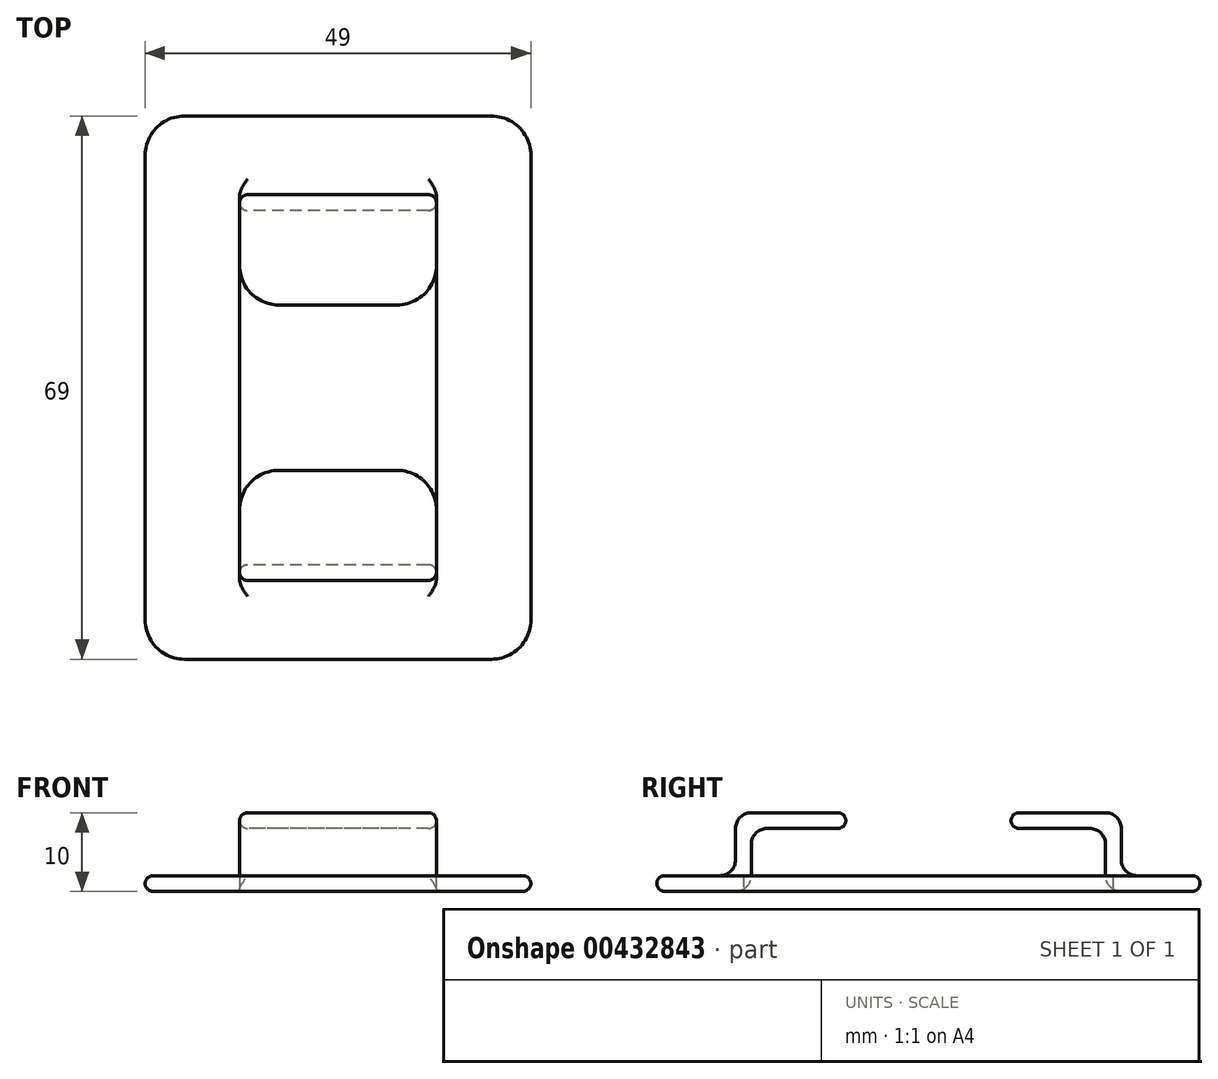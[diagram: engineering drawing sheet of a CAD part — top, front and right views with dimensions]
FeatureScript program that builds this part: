
annotation { "Feature Type Name" : "Feature", "Feature Type Description" : "" }
export const myFeature = defineFeature(function(context is Context, id is Id, definition is map)
    precondition{}
    {
        {
            var Q0;
            Q0=qCreatedBy(makeId("Right.planeOp"),FACE);
            var sketch = newSketch(context, id + "F0", { "sketchPlane" : qUnion([Q0])});
            skLineSegment(sketch, "E0.bottom", {"start": v(22.5, 3) * mm, "end": v(-22.5, 3) * mm, "construction": true});
            skLineSegment(sketch, "E0.top", {"start": v(22.5, -3) * mm, "end": v(-22.5, -3) * mm, "construction": true});
            skLineSegment(sketch, "E0.left", {"start": v(22.5, 3) * mm, "end": v(22.5, -3) * mm, "construction": true});
            skLineSegment(sketch, "E0.right", {"start": v(-22.5, 3) * mm, "end": v(-22.5, -3) * mm, "construction": true});
            skPoint(sketch, "E0.middle", {"position": v(0, 0) * mm});
            skLineSegment(sketch, "E1.bottom", {"start": v(20.5, 3) * mm, "end": v(10.5, 3) * mm});
            skLineSegment(sketch, "E1.top", {"start": v(22.5, 5) * mm, "end": v(10.5, 5) * mm});
            skLineSegment(sketch, "E1.right", {"start": v(10.5, 3) * mm, "end": v(10.5, 5) * mm});
            skLineSegment(sketch, "E2.bottom", {"start": v(-20.5, 3) * mm, "end": v(-10.5, 3) * mm});
            skLineSegment(sketch, "E2.top", {"start": v(-22.5, 5) * mm, "end": v(-10.5, 5) * mm});
            skLineSegment(sketch, "E2.right", {"start": v(-10.5, 3) * mm, "end": v(-10.5, 5) * mm});
            skLineSegment(sketch, "E3.bottom", {"start": v(26.5, -3) * mm, "end": v(34.5, -3) * mm});
            skLineSegment(sketch, "E3.top", {"start": v(24.5, -5) * mm, "end": v(34.5, -5) * mm});
            skLineSegment(sketch, "E3.left", {"start": v(22.5, -3) * mm, "end": v(22.5, -3) * mm});
            skLineSegment(sketch, "E3.right", {"start": v(34.5, -3) * mm, "end": v(34.5, -5) * mm});
            skLineSegment(sketch, "E4.bottom", {"start": v(-26.5, -3) * mm, "end": v(-34.5, -3) * mm});
            skLineSegment(sketch, "E4.top", {"start": v(-24.5, -5) * mm, "end": v(-34.5, -5) * mm});
            skLineSegment(sketch, "E4.left", {"start": v(-22.5, -3) * mm, "end": v(-22.5, -3) * mm});
            skLineSegment(sketch, "E4.right", {"start": v(-34.5, -3) * mm, "end": v(-34.5, -5) * mm});
            skLineSegment(sketch, "E5.bottom", {"start": v(22.5, 5) * mm, "end": v(22.5, 5) * mm});
            skLineSegment(sketch, "E5.left", {"start": v(22.5, 1) * mm, "end": v(22.5, -3) * mm});
            skLineSegment(sketch, "E5.right", {"start": v(24.5, 3) * mm, "end": v(24.5, -1) * mm});
            skLineSegment(sketch, "E6.bottom", {"start": v(-22.5, 5) * mm, "end": v(-22.5, 5) * mm});
            skLineSegment(sketch, "E6.left", {"start": v(-22.5, 1) * mm, "end": v(-22.5, -3) * mm});
            skLineSegment(sketch, "E6.right", {"start": v(-24.5, 3) * mm, "end": v(-24.5, -1) * mm});
            skPoint(sketch, "E7.visualSharp", {"position": v(22.5, 3) * mm});
            skArc(sketch, "E7.filletArc", {"start": v(22.5, 1) * mm, "mid": v(21.91, 2.41) * mm, "end": v(20.5, 3) * mm});
            skPoint(sketch, "E8.visualSharp", {"position": v(24.5, 5) * mm});
            skArc(sketch, "E8.filletArc", {"start": v(24.5, 3) * mm, "mid": v(23.91, 4.41) * mm, "end": v(22.5, 5) * mm});
            skPoint(sketch, "E9.visualSharp", {"position": v(24.5, -3) * mm});
            skArc(sketch, "E9.filletArc", {"start": v(24.5, -1) * mm, "mid": v(25.09, -2.41) * mm, "end": v(26.5, -3) * mm});
            skPoint(sketch, "E10.visualSharp", {"position": v(22.5, -5) * mm});
            skArc(sketch, "E10.filletArc", {"start": v(22.5, -3) * mm, "mid": v(23.09, -4.41) * mm, "end": v(24.5, -5) * mm});
            skPoint(sketch, "E11.visualSharp", {"position": v(-24.5, 5) * mm});
            skArc(sketch, "E11.filletArc", {"start": v(-22.5, 5) * mm, "mid": v(-23.91, 4.41) * mm, "end": v(-24.5, 3) * mm});
            skArc(sketch, "E12.filletArc", {"start": v(-20.5, 3) * mm, "mid": v(-21.91, 2.41) * mm, "end": v(-22.5, 1) * mm});
            skPoint(sketch, "E13.visualSharp", {"position": v(-24.5, -3) * mm});
            skArc(sketch, "E13.filletArc", {"start": v(-26.5, -3) * mm, "mid": v(-25.09, -2.41) * mm, "end": v(-24.5, -1) * mm});
            skPoint(sketch, "E14.visualSharp", {"position": v(-22.5, -5) * mm});
            skArc(sketch, "E14.filletArc", {"start": v(-24.5, -5) * mm, "mid": v(-23.09, -4.41) * mm, "end": v(-22.5, -3) * mm});
            skSolve(sketch);
        }
        {
            var Q0;
            Q0 = qSketchRegion(id + "F0", true);
            extrude(context, id + "F1", {"entities" : qUnion([Q0]), "depth" : 25 * mm});
        }
        {
            var Q0;
            Q0=makeQuery(id+"F1.opExtrude","CAP_FACE",FACE,{"disambiguationData":[OSD([sQuery(id+"F0.wireOp",EDGE,"E2.bottom"),sQuery(id+"F0.wireOp",EDGE,"E2.top"),sQuery(id+"F0.wireOp",EDGE,"E2.right"),sQuery(id+"F0.wireOp",EDGE,"E4.bottom"),sQuery(id+"F0.wireOp",EDGE,"E4.top"),sQuery(id+"F0.wireOp",EDGE,"E4.right"),sQuery(id+"F0.wireOp",EDGE,"E6.left"),sQuery(id+"F0.wireOp",EDGE,"E6.right"),sQuery(id+"F0.wireOp",EDGE,"E11.filletArc"),sQuery(id+"F0.wireOp",EDGE,"E12.filletArc"),sQuery(id+"F0.wireOp",EDGE,"E13.filletArc"),sQuery(id+"F0.wireOp",EDGE,"E14.filletArc")])],"isStart":false});
            var sketch = newSketch(context, id + "F2", { "sketchPlane" : qUnion([Q0])});
            skLineSegment(sketch, "E15.bottom", {"start": v(-34.5, -5) * mm, "end": v(34.5, -5) * mm});
            skLineSegment(sketch, "E15.top", {"start": v(-34.5, -3) * mm, "end": v(34.5, -3) * mm});
            skLineSegment(sketch, "E15.left", {"start": v(-34.5, -5) * mm, "end": v(-34.5, -3) * mm});
            skLineSegment(sketch, "E15.right", {"start": v(34.5, -5) * mm, "end": v(34.5, -3) * mm});
            skSolve(sketch);
        }
        {
            var Q0;
            Q0 = qSketchRegion(id + "F2", true);
            extrude(context, id + "F3", {"entities" : qUnion([Q0]), "operationType" : NewBodyOperationType.ADD, "depth" : 12 * mm});
        }
        {
            var Q0;
            Q0=makeQuery(id+"F1.opExtrude","CAP_FACE",FACE,{"disambiguationData":[OSD([sQuery(id+"F0.wireOp",EDGE,"E1.bottom"),sQuery(id+"F0.wireOp",EDGE,"E1.top"),sQuery(id+"F0.wireOp",EDGE,"E1.right"),sQuery(id+"F0.wireOp",EDGE,"E3.bottom"),sQuery(id+"F0.wireOp",EDGE,"E3.top"),sQuery(id+"F0.wireOp",EDGE,"E3.right"),sQuery(id+"F0.wireOp",EDGE,"E5.left"),sQuery(id+"F0.wireOp",EDGE,"E5.right"),sQuery(id+"F0.wireOp",EDGE,"E7.filletArc"),sQuery(id+"F0.wireOp",EDGE,"E8.filletArc"),sQuery(id+"F0.wireOp",EDGE,"E9.filletArc"),sQuery(id+"F0.wireOp",EDGE,"E10.filletArc")])],"isStart":true});
            var sketch = newSketch(context, id + "F4", { "sketchPlane" : qUnion([Q0])});
            skLineSegment(sketch, "E16.bottom", {"start": v(-34.5, -5) * mm, "end": v(34.5, -5) * mm});
            skLineSegment(sketch, "E16.top", {"start": v(-34.5, -3) * mm, "end": v(34.5, -3) * mm});
            skLineSegment(sketch, "E16.left", {"start": v(-34.5, -5) * mm, "end": v(-34.5, -3) * mm});
            skLineSegment(sketch, "E16.right", {"start": v(34.5, -5) * mm, "end": v(34.5, -3) * mm});
            skSolve(sketch);
        }
        {
            var Q0;
            Q0 = qSketchRegion(id + "F4", true);
            extrude(context, id + "F5", {"entities" : qUnion([Q0]), "operationType" : NewBodyOperationType.ADD, "depth" : 12 * mm});
        }
        {
            var Q0;
            Q0=makeQuery(id+"F5.opExtrude","CAP_EDGE",EDGE,{"disambiguationData":[OSD([sQuery(id+"F4.wireOp",EDGE,"E16.left")])],"isStart":false});
            var Q1;
            Q1=makeQuery(id+"F3.opExtrude","CAP_EDGE",EDGE,{"disambiguationData":[OSD([sQuery(id+"F2.wireOp",EDGE,"E15.right")])],"isStart":false});
            var Q2;
            Q2=makeQuery(id+"F3.opExtrude","CAP_EDGE",EDGE,{"disambiguationData":[OSD([sQuery(id+"F2.wireOp",EDGE,"E15.left")])],"isStart":false});
            var Q3;
            Q3=makeQuery(id+"F5.opExtrude","CAP_EDGE",EDGE,{"disambiguationData":[OSD([sQuery(id+"F4.wireOp",EDGE,"E16.right")])],"isStart":false});
            var Q4;
            Q4=makeQuery(id+"F1.opExtrude","CAP_EDGE",EDGE,{"disambiguationData":[OSD([sQuery(id+"F0.wireOp",EDGE,"E1.right")])],"isStart":true});
            var Q5;
            Q5=makeQuery(id+"F1.opExtrude","CAP_EDGE",EDGE,{"disambiguationData":[OSD([sQuery(id+"F0.wireOp",EDGE,"E1.right")])],"isStart":false});
            var Q6;
            Q6=makeQuery(id+"F1.opExtrude","CAP_EDGE",EDGE,{"disambiguationData":[OSD([sQuery(id+"F0.wireOp",EDGE,"E2.right")])],"isStart":false});
            var Q7;
            Q7=makeQuery(id+"F1.opExtrude","CAP_EDGE",EDGE,{"disambiguationData":[OSD([sQuery(id+"F0.wireOp",EDGE,"E2.right")])],"isStart":true});
            fillet(context, id + "F6", {"entities" : qUnion([Q0, Q1, Q2, Q3, Q4, Q5, Q6, Q7]), "radius" : 5 * mm, "tangentPropagation" : true, "allowEdgeOverflow" : false});
        }
        {
            var Q0;
            Q0=makeQuery(id+"F5.opExtrude","CAP_EDGE",EDGE,{"disambiguationData":[OSD([sQuery(id+"F4.wireOp",EDGE,"E16.bottom")])],"isStart":false});
            var Q1;
            Q1=makeQuery(id+"F5.opExtrude","CAP_EDGE",EDGE,{"disambiguationData":[OSD([sQuery(id+"F4.wireOp",EDGE,"E16.top")])],"isStart":false});
            var Q2;
            Q2=makeQuery(id+"F1.opExtrude","CAP_EDGE",EDGE,{"disambiguationData":[OSD([sQuery(id+"F0.wireOp",EDGE,"E2.top")])],"isStart":false});
            var Q3;
            Q3=makeQuery(id+"F1.opExtrude","CAP_EDGE",EDGE,{"disambiguationData":[OSD([sQuery(id+"F0.wireOp",EDGE,"E1.top")])],"isStart":false});
            var Q4;
            Q4=makeQuery(id+"F1.opExtrude","SWEPT_EDGE",EDGE,{"disambiguationData":[OSD([sQuery(id+"F0.wireOp",EDGE,"E2.bottom"),sQuery(id+"F0.wireOp",EDGE,"E2.right")])]});
            var Q5;
            Q5=makeQuery(id+"F1.opExtrude","SWEPT_EDGE",EDGE,{"disambiguationData":[OSD([sQuery(id+"F0.wireOp",EDGE,"E1.bottom"),sQuery(id+"F0.wireOp",EDGE,"E1.right")])]});
            fillet(context, id + "F7", {"entities" : qUnion([Q0, Q1, Q2, Q3, Q4, Q5]), "radius" : 1 * mm, "tangentPropagation" : true, "allowEdgeOverflow" : false});
        }
    });
